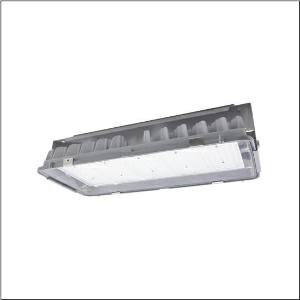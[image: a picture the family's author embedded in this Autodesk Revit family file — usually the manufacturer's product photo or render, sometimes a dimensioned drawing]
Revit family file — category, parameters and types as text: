
# Revit family: highbay_11xtreme_51hf62da4hma
name_source: partatom
category: Lighting Fixtures
units: mm (PartAtom-declared; Revit-internal decimal feet)

## family parameters
Cut with Voids When Loaded = No
Host = Face
Light Source = No
Part Type = Normal
Room Calculation Point = No
Round Connector Dimension = Use Diameter
Shared = No

## types (1)
- --- (1 x LED, 18500 lm, 96.5 W, 4000K)
    Apparent Load = 97 VA
    CIE Flux Codes = 84 96 100 100 100
    Color Rendering = 80
    Color Temperature = 4000K
    Default Elevation = 1800 mm
    Description = Highbay 11Xtreme, LED high bay luminaire, primary light control with lens, of PMMA, primary optical cover: cover, of toughened safety glass, light emission: direct distribution, primary light characteristic: symmetric, installation type: suspended mounting, surface-mounted, 1x LED module,for 1x LED, rated luminous flux: 18.500lm, luminous efficacy: 192lm/W, light colour: 840, colour temperature: 4000K, with cable H07RN-F 5x 1.5mm², mains connection: 220..240V, AC, 50/60Hz, cable length: 1,5m, rated input power: 97W, luminaire housing, of diecast aluminium, coated, silver, length: 595mm, width: 280mm, height: 195mm, protection rating (complete): IP66, insulation class (complete): insulation class I (protective earthing), certification: CE, ENEC, UKCA, protection symbol: D, ball protection: ball impact resistant according to DIN VDE 0710 part 13 (with chain suspension), impact resistance: IK08, permissible operating ambient temperature: -25..+70°C, reducing of maximum allowable ambient temperature of 5°C with ceiling mounting, packaging unit: 1 piece
    Height = 157 mm
    Lamp = 1 x LED
    Lamp Light Flux = 18500 lm
    Lamp Power = 96.5 W
    Lamp count = 1
    Length = 593 mm
    Luminous efficacy = 192 lm/W
    Manufacturer = Siteco
    ModVariant = No
    Model = 51HF62DA4HMA
    Mounting Place = Ceiling
    Mounting Type = Pendant
    Number of Poles = 1
    OnlyDefault = Yes
    Power Factor = 1
    Product Name = Highbay 11Xtreme
    Product group = LED high bay luminaire
    ProductGroupID = 903
    Protection Class = Protection class I
    Protection Degree = IP 66
    RLX_Detail_Level = 1
    RLX_Emergency_Light_Flux = 0 lm
    RLX_Emergency_Type = 0
    RLX_Emergency_Type_DB = No
    RlxData = <blob elided: 28257 chars, md5=ddde446d>
    Socket = socket
    Standby Power = 0 W
    System Light Flux = 18500 lm
    System Power = 97 W
    Type Comments = factory setting: luminous flux: 100 % | dim-lin: 254 | 652 mA
    Type Image = l_1258342.jpg
    URL = http://relux.com
    VarID = @adj_035713
    Voltage = 0 V
    Weight = 0.00 kg
    Width = 568 mm

## geometry (parser evidence)
native form markers: Blend x4, Sweep x10
no freeform markers — native parametric forms only
